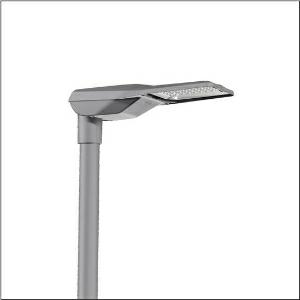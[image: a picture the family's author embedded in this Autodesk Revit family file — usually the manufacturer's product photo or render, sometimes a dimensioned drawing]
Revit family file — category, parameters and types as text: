
# Revit family: streetlight_sl_21_iq_mini___st0_8a_5xe2c31d08hb_f94e
name_source: partatom
category: Lighting Fixtures
units: mm (PartAtom-declared; Revit-internal decimal feet)

## family parameters
Cut with Voids When Loaded = No
Host = Face
Light Source = No
Part Type = Normal
Room Calculation Point = No
Round Connector Dimension = Use Diameter
Shared = No

## types (1)
- --- (1 x LED, 9450 lm, 70.9 W, 3000K)
    Apparent Load = 71 VA
    CIE Flux Codes = 38 75 97 100 100
    Color Rendering = 70
    Color Temperature = 3000K
    Default Elevation = 1800 mm
    Description = Streetlight SL 21 mini, mast luminaire, primary light control with lens, of PMMA, primary optical cover: cover, of toughened safety glass, transparent, light distribution: ST0.8a, light emission: direct distribution, primary light characteristic: asymmetric, installation type: post-top, side-entry, LED, High Power LED, rated luminous flux: 9.450lm, luminous efficacy: 133lm/W, light colour: 730, colour temperature: 3000K, control gear: ECG iQ, control: Auto-Match, Temp-Guard, Lumen-Switch, Night-Set, Smart-Wire, Light-Fading, Desk-Remote (wireless, voltage-free reading and setting of iQ features in the workshop via application-optimized NFC function/RFID function), optimised constant luminous flux control (CLO 2.0), mains connection: 220..240V, AC, 50/60Hz, start of lifetime: 71W, end of lifetime: 75W, reduction: 31W, luminaire housing, of diecast aluminium, powder-coated, Siteco® metallic grey (DB 702S), corrosivity category C5 according to DIN EN ISO 12944, length: 628mm, width: 235mm, height: 110mm, spigot size: 60/76mm (post-top) and 42/60/76mm (side-entry), mast flange for spigot size: 42mm: 5XC10008XM4, 60mm: 5XC10008XM2, 76/60mm: 5XC10108XM1, protection rating (complete): IP66, insulation class (complete): insulation class II (safety insulation), certification: CE, ENEC, VDE, impact resistance: IK09, permissible operating ambient temperature for outdoor applications: -40..+50°C, standard-compliant lighting for roads and squares, packaging unit: 1 piece

Light Distribution: ST0.8a
    Height = 110 mm
    Lamp = 1 x LED
    Lamp Light Flux = 9450 lm
    Lamp Power = 70.9 W
    Lamp count = 1
    Length = 625 mm
    Luminous efficacy = 133 lm/W
    Manufacturer = Siteco
    ModVariant = No
    Model = 5XE2C31D08HB
    Number of Poles = 1
    OnlyDefault = Yes
    Power Factor = 1
    Product Name = Streetlight SL 21 iQ mini | ST0.8a
    Product group = mast luminaire | pylon top
    ProductGroupID = 6100
    Protection Class = Protection class II
    Protection Degree = IP 66
    RLX_Detail_Level = 1
    RlxData = <blob elided: 93773 chars, md5=20426ab4>
    Socket = socket
    Standby Power = 0 W
    System Light Flux = 9450 lm
    System Power = 71 W
    Type Comments = factory setting: luminous flux: 100 % | dim-lin: 254 | 711 mA
    Type Image = l_1003519.jpg
    URL = http://relux.com
    VarID = @adj_068695
    Voltage = 0 V
    Weight = 0.00 kg
    Width = 234 mm

## geometry (parser evidence)
native form markers: Blend x4, Sweep x11
no freeform markers — native parametric forms only
